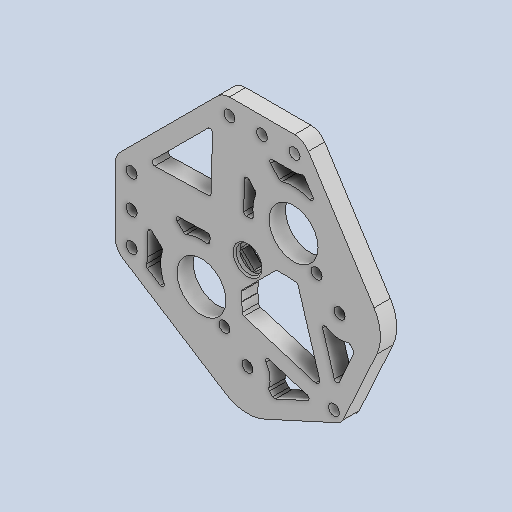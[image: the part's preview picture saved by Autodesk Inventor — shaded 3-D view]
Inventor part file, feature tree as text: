
AUTODESK INVENTOR PART (.ipt)
format: ipt  version: 2022 (Build 260153000, 153)  size: 372,736 bytes
history: native  units: in
note: dims shown in document units (in); Inventor stores cm internally (conversion verified against a paired STEP export)
features: sketch x5, other x3
ambient origin geometry x8: Origin, YZ Plane, XZ Plane, XY Plane, X Axis, Y Axis, Z Axis, Center Point
bodies: Solid1 (feature_tree)
feature tree (8):
  other  "motorplate.ipt"
  other  "Solid1::motorplate.ipt"
  other  "TaggingFeature1"
  sketch  "Sketch1"  dims[d0=0.3937in]
  sketch  "Sketch2"
  sketch  "Sketch3"
  sketch  "Sketch4"
  sketch  "Sketch5"
